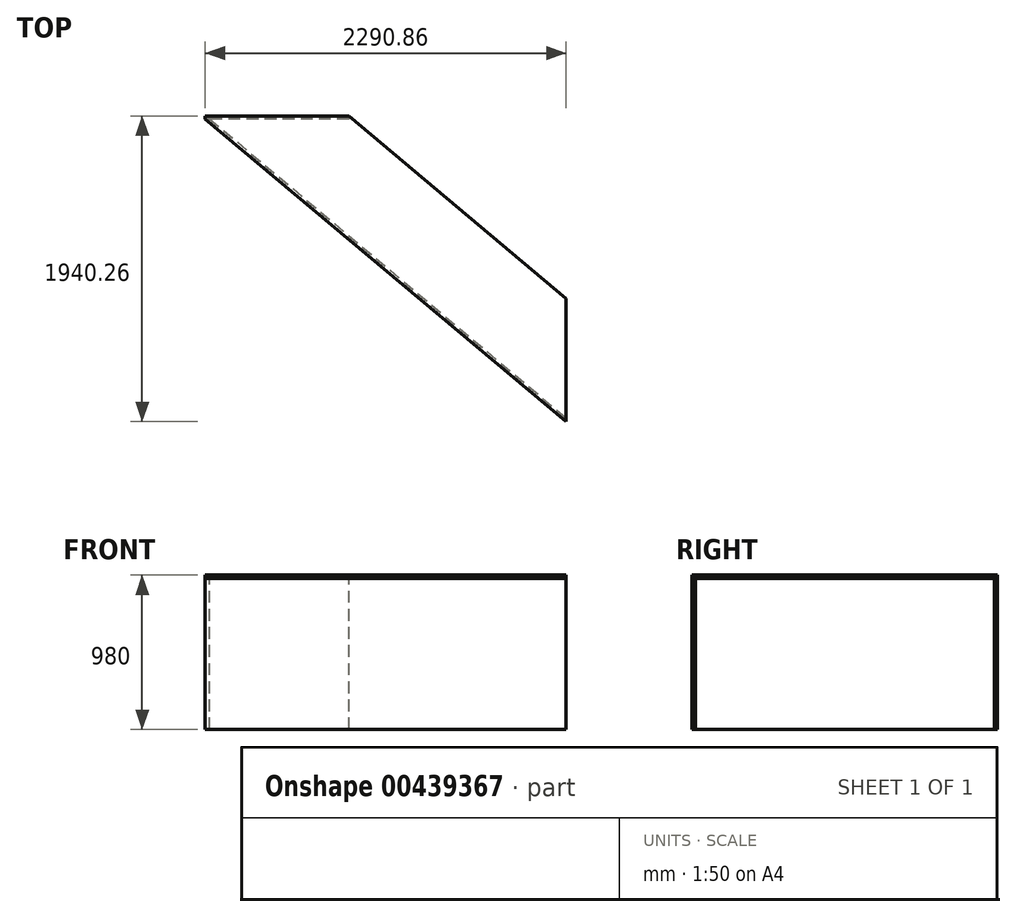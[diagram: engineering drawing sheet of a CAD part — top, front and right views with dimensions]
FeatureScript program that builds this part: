
annotation { "Feature Type Name" : "Feature", "Feature Type Description" : "" }
export const myFeature = defineFeature(function(context is Context, id is Id, definition is map)
    precondition{}
    {
        {
            assignVariable(context, id + "F0", {"name" : "hoogte", "anyValue" : 960});
        }
        {
            var Q0;
            Q0=qCreatedBy(makeId("Top.planeOp"),FACE);
            var sketch = newSketch(context, id + "F1", { "sketchPlane" : qUnion([Q0])});
            skLineSegment(sketch, "E0", {"start": v(0, 0) * mm, "end": v(0, 783.24) * mm});
            skLineSegment(sketch, "E1", {"start": v(0, 783.24) * mm, "end": v(-1378.88, 1940.26) * mm});
            skLineSegment(sketch, "E2", {"start": v(-1378.88, 1940.26) * mm, "end": v(-2290.86, 1940.26) * mm});
            skLineSegment(sketch, "E3", {"start": v(-2290.86, 1922.26) * mm, "end": v(0, 0) * mm});
            skLineSegment(sketch, "E4.0", {"start": v(-2262.86, 1922.26) * mm, "end": v(0, 23.5) * mm});
            skLineSegment(sketch, "E4.2", {"start": v(-1357.43, 1922.26) * mm, "end": v(-2290.86, 1922.26) * mm});
            skLineSegment(sketch, "E5", {"start": v(-2290.86, 1922.26) * mm, "end": v(-2290.86, 1940.26) * mm});
            skLineSegment(sketch, "E6", {"start": v(-1378.88, 1940.26) * mm, "end": v(-1378.88, 1922.26) * mm});
            skSolve(sketch);
        }
        {
            var Q0;
            {var subQ0=sQuery(id+"F1.wireOp",EDGE,"E4.0");Q0=makeQuery(id+"F1.imprint","IMPRINT",FACE,{"disambiguationData":[TD([[makeQuery(id+"F1.imprint","IMPRINT",EDGE,{"derivedFrom":subQ0}),1.0]])]});}
            var Q1;
            {var subQ0=sQuery(id+"F1.wireOp",EDGE,"E2");Q1=makeQuery(id+"F1.imprint","IMPRINT",FACE,{"disambiguationData":[TD([[makeQuery(id+"F1.imprint","IMPRINT",EDGE,{"derivedFrom":subQ0}),1.0]])]});}
            var Q2;
            {var subQ0=sQuery(id+"F1.wireOp",EDGE,"E3");Q2=makeQuery(id+"F1.imprint","IMPRINT",FACE,{"disambiguationData":[TD([[makeQuery(id+"F1.imprint","IMPRINT",EDGE,{"derivedFrom":subQ0}),1.0]])]});}
            var Q3;
            {var subQ0=sQuery(id+"F1.wireOp",EDGE,"E6");Q3=makeQuery(id+"F1.imprint","IMPRINT",FACE,{"disambiguationData":[TD([[makeQuery(id+"F1.imprint","IMPRINT",EDGE,{"derivedFrom":subQ0}),1.0]])]});}
            extrude(context, id + "F2", {"entities" : qUnion([Q0, Q1, Q2, Q3]), "depth" : 20 * mm});
        }
        {
            var Q0;
            {var subQ0=sQuery(id+"F1.wireOp",EDGE,"E2");Q0=makeQuery(id+"F1.imprint","IMPRINT",FACE,{"disambiguationData":[TD([[makeQuery(id+"F1.imprint","IMPRINT",EDGE,{"derivedFrom":subQ0}),1.0]])]});}
            extrude(context, id + "F3", {"entities" : qUnion([Q0]), "oppositeDirection" : true, "depth" : (getVariable(context, 'hoogte')) * mm});
        }
        {
            var Q0;
            {var subQ0=sQuery(id+"F1.wireOp",EDGE,"E3");Q0=makeQuery(id+"F1.imprint","IMPRINT",FACE,{"disambiguationData":[TD([[makeQuery(id+"F1.imprint","IMPRINT",EDGE,{"derivedFrom":subQ0}),1.0]])]});}
            extrude(context, id + "F4", {"entities" : qUnion([Q0]), "oppositeDirection" : true, "depth" : (getVariable(context, 'hoogte')) * mm});
        }
    });
